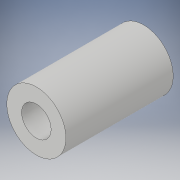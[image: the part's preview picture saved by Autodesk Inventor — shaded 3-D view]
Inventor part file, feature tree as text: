
AUTODESK INVENTOR PART (.ipt)
format: ipt  version: 2017 (Build 210142000, 142)  size: 94,208 bytes
history: native  units: in
note: dims shown in document units (in); Inventor stores cm internally (conversion verified against a paired STEP export)
features: extrude x1, sketch x1
ambient origin geometry x8: Origin, YZ Plane, XZ Plane, XY Plane, X Axis, Y Axis, Z Axis, Center Point
bodies: Solid1 (feature_tree)
feature tree (2):
  extrude  "Extrusion1"  Depth=0.69in
  sketch  "Sketch1"  dims[d0=0.19in d1=0.38in d2=0.69in d3=0.0in]
